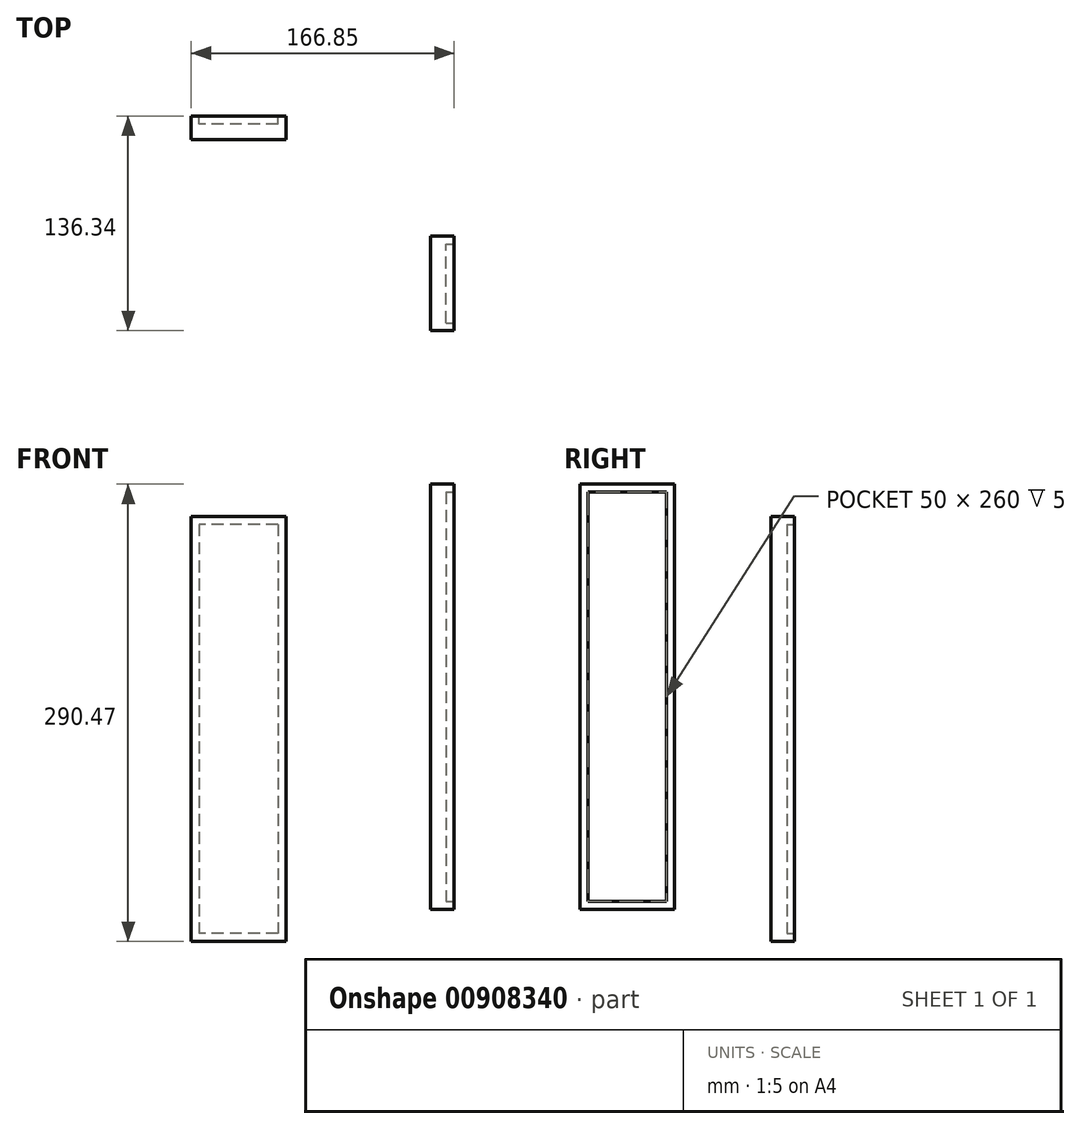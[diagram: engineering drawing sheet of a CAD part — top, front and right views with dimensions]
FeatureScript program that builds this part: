
annotation { "Feature Type Name" : "Feature", "Feature Type Description" : "" }
export const myFeature = defineFeature(function(context is Context, id is Id, definition is map)
    precondition{}
    {
        {
            var Q0;
            Q0=qCreatedBy(makeId("Front.planeOp"),FACE);
            var sketch = newSketch(context, id + "F0", { "sketchPlane" : qUnion([Q0])});
            skPoint(sketch, "E0.middle", {"position": v(0, 0) * mm});
            skLineSegment(sketch, "E1.bottom", {"start": v(-151.85, 109.1) * mm, "end": v(-91.85, 109.1) * mm});
            skLineSegment(sketch, "E1.top", {"start": v(-151.85, -160.9) * mm, "end": v(-91.85, -160.9) * mm});
            skLineSegment(sketch, "E1.left", {"start": v(-151.85, 109.1) * mm, "end": v(-151.85, -160.9) * mm});
            skLineSegment(sketch, "E1.right", {"start": v(-91.85, 109.1) * mm, "end": v(-91.85, -160.9) * mm});
            skSolve(sketch);
        }
        {
            var Q0;
            Q0=qCreatedBy(makeId("Right.planeOp"),FACE);
            var sketch = newSketch(context, id + "F1", { "sketchPlane" : qUnion([Q0])});
            skLineSegment(sketch, "E2.bottom", {"start": v(-136.34, 129.58) * mm, "end": v(-76.34, 129.58) * mm});
            skLineSegment(sketch, "E2.top", {"start": v(-136.34, -140.42) * mm, "end": v(-76.34, -140.42) * mm});
            skLineSegment(sketch, "E2.left", {"start": v(-136.34, 129.58) * mm, "end": v(-136.34, -140.42) * mm});
            skLineSegment(sketch, "E2.right", {"start": v(-76.34, 129.58) * mm, "end": v(-76.34, -140.42) * mm});
            skSolve(sketch);
        }
        {
            var Q0;
            Q0 = qSketchRegion(id + "F0", true);
            extrude(context, id + "F2", {"entities" : qUnion([Q0]), "depth" : 15 * mm, "offsetDistance" : 25 * mm});
        }
        {
            var Q0;
            Q0=makeQuery(id+"F0.imprint","IMPRINT",FACE,{"disambiguationData":[TD([[makeQuery(id+"F0.imprint","IMPRINT",EDGE,{"derivedFrom":sQuery(id+"F0.wireOp",EDGE,"E1.bottom")}),-1.0]])]});
            var sketch = newSketch(context, id + "F3", { "sketchPlane" : qUnion([Q0])});
            skLineSegment(sketch, "E3.bottom", {"start": v(-96.85, 104.1) * mm, "end": v(-146.85, 104.1) * mm});
            skLineSegment(sketch, "E3.top", {"start": v(-96.85, -155.9) * mm, "end": v(-146.85, -155.9) * mm});
            skLineSegment(sketch, "E3.left", {"start": v(-96.85, 104.1) * mm, "end": v(-96.85, -155.9) * mm});
            skLineSegment(sketch, "E3.right", {"start": v(-146.85, 104.1) * mm, "end": v(-146.85, -155.9) * mm});
            skSolve(sketch);
        }
        {
            var Q0;
            Q0=makeQuery(id+"F3.imprint","IMPRINT",FACE,{"disambiguationData":[TD([[makeQuery(id+"F3.imprint","IMPRINT",EDGE,{"derivedFrom":sQuery(id+"F3.wireOp",EDGE,"E3.bottom")}),1.0]])]});
            extrude(context, id + "F4", {"entities" : qUnion([Q0]), "operationType" : NewBodyOperationType.ADD, "depth" : -5 * mm, "offsetDistance" : 25 * mm});
        }
        {
            var Q0;
            Q0 = qSketchRegion(id + "F1", true);
            extrude(context, id + "F5", {"entities" : qUnion([Q0]), "depth" : 15 * mm, "offsetDistance" : 25 * mm});
        }
        {
            var Q0;
            Q0=makeQuery(id+"F5.opExtrude","CAP_FACE",FACE,{"disambiguationData":[OSD([sQuery(id+"F1.wireOp",EDGE,"E2.bottom"),sQuery(id+"F1.wireOp",EDGE,"E2.top"),sQuery(id+"F1.wireOp",EDGE,"E2.left"),sQuery(id+"F1.wireOp",EDGE,"E2.right")])],"isStart":false});
            var sketch = newSketch(context, id + "F6", { "sketchPlane" : qUnion([Q0])});
            skLineSegment(sketch, "E4.bottom", {"start": v(-131.34, 124.58) * mm, "end": v(-81.34, 124.58) * mm});
            skLineSegment(sketch, "E4.top", {"start": v(-131.34, -135.42) * mm, "end": v(-81.34, -135.42) * mm});
            skLineSegment(sketch, "E4.left", {"start": v(-131.34, 124.58) * mm, "end": v(-131.34, -135.42) * mm});
            skLineSegment(sketch, "E4.right", {"start": v(-81.34, 124.58) * mm, "end": v(-81.34, -135.42) * mm});
            skSolve(sketch);
        }
        {
            var Q0;
            Q0=makeQuery(id+"F6.imprint","IMPRINT",FACE,{"disambiguationData":[TD([[makeQuery(id+"F6.imprint","IMPRINT",EDGE,{"derivedFrom":sQuery(id+"F6.wireOp",EDGE,"E4.bottom")}),-1.0]])]});
            extrude(context, id + "F7", {"entities" : qUnion([Q0]), "operationType" : NewBodyOperationType.REMOVE, "oppositeDirection" : true, "depth" : 5 * mm, "offsetDistance" : 25 * mm});
        }
        {
            var Q0;
            Q0=makeQuery(id+"F4.opExtrude","CAP_FACE",FACE,{"disambiguationData":[OSD([sQuery(id+"F3.wireOp",EDGE,"E3.bottom"),sQuery(id+"F3.wireOp",EDGE,"E3.top"),sQuery(id+"F3.wireOp",EDGE,"E3.left"),sQuery(id+"F3.wireOp",EDGE,"E3.right")])],"isStart":false});
            var sketch = newSketch(context, id + "F8", { "sketchPlane" : qUnion([Q0])});
            skLineSegment(sketch, "E5.bottom", {"start": v(133.85, -150.9) * mm, "end": v(109.85, -150.9) * mm});
            skLineSegment(sketch, "E5.top", {"start": v(133.85, 99.1) * mm, "end": v(109.85, 99.1) * mm});
            skLineSegment(sketch, "E5.left", {"start": v(133.85, -150.9) * mm, "end": v(133.85, 99.1) * mm});
            skLineSegment(sketch, "E5.right", {"start": v(109.85, -150.9) * mm, "end": v(109.85, 99.1) * mm});
            skEllipse(sketch, "E6", {"center": v(121.85, -25.9) * mm, "majorRadius": 25 * mm, "minorRadius": 20 * mm, "majorAxis": v(0, 1)});
            skSolve(sketch);
        }
        {
            var Q0;
            Q0=makeQuery(id+"F8.imprint","IMPRINT",FACE,{"disambiguationData":[TD([[makeQuery(id+"F8.imprint","IMPRINT",EDGE,{"derivedFrom":sQuery(id+"F8.wireOp",EDGE,"E5.bottom")}),-1.0]])]});
            var Q1;
            {var subQ0=sQuery(id+"F8.wireOp",EDGE,"E5.right");var subQ1=sQuery(id+"F8.wireOp",EDGE,"E5.top");var subQ2=makeQuery(id+"F8.imprint","INTERSECT",VERTEX,{"derivedFrom":[subQ1,subQ0]});Q1=makeQuery(id+"F8.imprint","IMPRINT",FACE,{"disambiguationData":[TD([[makeQuery(id+"F8.imprint","IMPRINT",EDGE,{"disambiguationData":[TD([[subQ2,1.0]])],"derivedFrom":subQ1}),1.0]])]});}
            var Q2;
            {var subQ0=sQuery(id+"F8.wireOp",EDGE,"E5.left");var subQ1=sQuery(id+"F8.wireOp",EDGE,"E5.top");var subQ2=makeQuery(id+"F8.imprint","INTERSECT",VERTEX,{"derivedFrom":[subQ1,subQ0]});Q2=makeQuery(id+"F8.imprint","IMPRINT",FACE,{"disambiguationData":[TD([[makeQuery(id+"F8.imprint","IMPRINT",EDGE,{"disambiguationData":[TD([[subQ2,-1.0]])],"derivedFrom":subQ1}),1.0]])]});}
            var Q3;
            {var subQ0=sQuery(id+"F8.wireOp",EDGE,"jjR4p86R-AGvj-MJNc-cVGU-iWlVXVb1kiAX");var subQ1=sQuery(id+"F8.wireOp",EDGE,"E5.right");var subQ2=makeQuery(id+"F8.imprint","INTERSECT",VERTEX,{"derivedFrom":[subQ1,subQ0]});Q3=makeQuery(id+"F8.imprint","IMPRINT",FACE,{"disambiguationData":[TD([[makeQuery(id+"F8.imprint","IMPRINT",EDGE,{"disambiguationData":[TD([[subQ2,-1.0]])],"derivedFrom":subQ1}),-1.0]])]});}
            var Q4;
            {var subQ0=sQuery(id+"F8.wireOp",EDGE,"jjR4p86R-AGvj-MJNc-cVGU-iWlVXVb1kiAX");var subQ1=sQuery(id+"F8.wireOp",EDGE,"E5.left");var subQ2=makeQuery(id+"F8.imprint","INTERSECT",VERTEX,{"derivedFrom":[subQ1,subQ0]});Q4=makeQuery(id+"F8.imprint","IMPRINT",FACE,{"disambiguationData":[TD([[makeQuery(id+"F8.imprint","IMPRINT",EDGE,{"disambiguationData":[TD([[subQ2,-1.0]])],"derivedFrom":subQ1}),1.0]])]});}
            var Q5;
            {var subQ0=sQuery(id+"F8.wireOp",EDGE,"jjR4p86R-AGvj-MJNc-cVGU-iWlVXVb1kiAX");var subQ1=sQuery(id+"F8.wireOp",EDGE,"E5.left");var subQ2=makeQuery(id+"F8.imprint","INTERSECT",VERTEX,{"derivedFrom":[subQ1,subQ0]});Q5=makeQuery(id+"F8.imprint","IMPRINT",FACE,{"disambiguationData":[TD([[makeQuery(id+"F8.imprint","IMPRINT",EDGE,{"disambiguationData":[TD([[subQ2,-1.0]])],"derivedFrom":subQ1}),-1.0]])]});}
            var Q6;
            {var subQ0=sQuery(id+"F8.wireOp",EDGE,"E6");var subQ1=sQuery(id+"F8.wireOp",EDGE,"E5.left");var subQ2=makeQuery(id+"F8.imprint","INTERSECT",VERTEX,{"disambiguationData":[OD(0.0)],"derivedFrom":[subQ1,subQ0]});Q6=makeQuery(id+"F8.imprint","IMPRINT",FACE,{"disambiguationData":[TD([[makeQuery(id+"F8.imprint","IMPRINT",EDGE,{"disambiguationData":[TD([[subQ2,-1.0]])],"derivedFrom":subQ1}),-1.0]])]});}
            var Q7;
            {var subQ0=sQuery(id+"F8.wireOp",EDGE,"E6");var subQ1=sQuery(id+"F8.wireOp",EDGE,"E5.left");var subQ2=makeQuery(id+"F8.imprint","INTERSECT",VERTEX,{"disambiguationData":[OD(0.0)],"derivedFrom":[subQ1,subQ0]});Q7=makeQuery(id+"F8.imprint","IMPRINT",FACE,{"disambiguationData":[TD([[makeQuery(id+"F8.imprint","IMPRINT",EDGE,{"disambiguationData":[TD([[subQ2,-1.0]])],"derivedFrom":subQ1}),1.0]])]});}
            var Q8;
            {var subQ0=sQuery(id+"F8.wireOp",EDGE,"E6");var subQ1=sQuery(id+"F8.wireOp",EDGE,"E5.right");var subQ2=makeQuery(id+"F8.imprint","INTERSECT",VERTEX,{"disambiguationData":[OD(0.0)],"derivedFrom":[subQ1,subQ0]});Q8=makeQuery(id+"F8.imprint","IMPRINT",FACE,{"disambiguationData":[TD([[makeQuery(id+"F8.imprint","IMPRINT",EDGE,{"disambiguationData":[TD([[subQ2,-1.0]])],"derivedFrom":subQ1}),-1.0]])]});}
            var Q9;
            {var subQ0=sQuery(id+"F8.wireOp",EDGE,"E6");var subQ1=sQuery(id+"F8.wireOp",EDGE,"E5.right");var subQ2=makeQuery(id+"F8.imprint","INTERSECT",VERTEX,{"disambiguationData":[OD(0.0)],"derivedFrom":[subQ1,subQ0]});Q9=makeQuery(id+"F8.imprint","IMPRINT",FACE,{"disambiguationData":[TD([[makeQuery(id+"F8.imprint","IMPRINT",EDGE,{"disambiguationData":[TD([[subQ2,-1.0]])],"derivedFrom":subQ1}),1.0]])]});}
            var Q10;
            {var subQ0=sQuery(id+"F8.wireOp",EDGE,"jjR4p86R-AGvj-MJNc-cVGU-iWlVXVb1kiAX");var subQ1=sQuery(id+"F8.wireOp",EDGE,"E5.right");var subQ2=makeQuery(id+"F8.imprint","INTERSECT",VERTEX,{"derivedFrom":[subQ1,subQ0]});Q10=makeQuery(id+"F8.imprint","IMPRINT",FACE,{"disambiguationData":[TD([[makeQuery(id+"F8.imprint","IMPRINT",EDGE,{"disambiguationData":[TD([[subQ2,-1.0]])],"derivedFrom":subQ1}),1.0]])]});}
            extrude(context, id + "F9", {"entities" : qUnion([Q0, Q1, Q2, Q3, Q4, Q5, Q6, Q7, Q8, Q9, Q10]), "operationType" : NewBodyOperationType.REMOVE, "oppositeDirection" : true, "depth" : 10 * mm, "offsetDistance" : 25 * mm});
        }
    });
